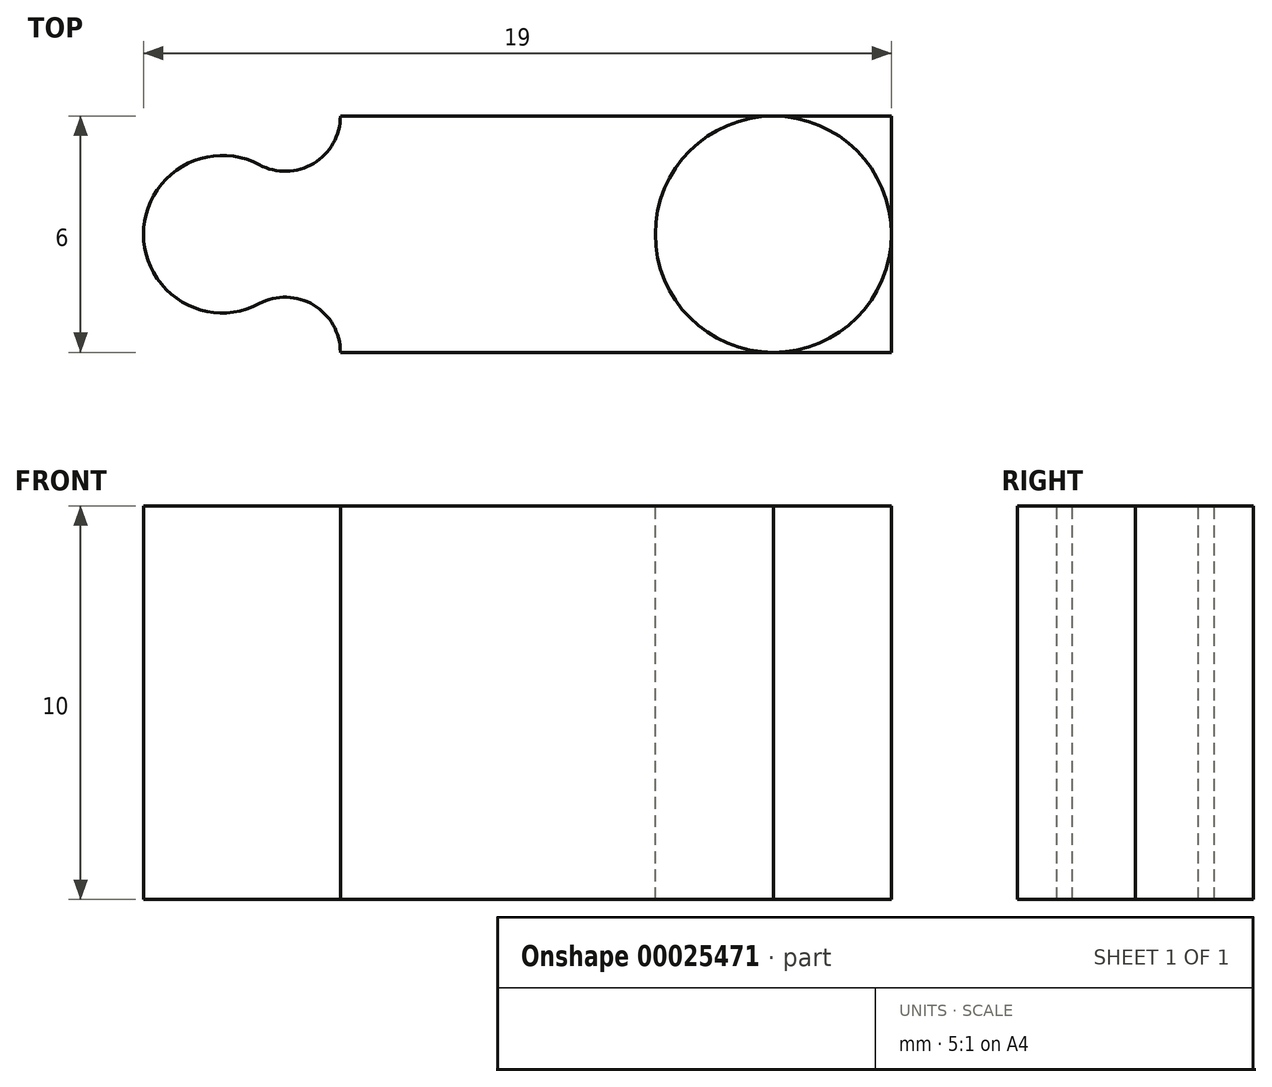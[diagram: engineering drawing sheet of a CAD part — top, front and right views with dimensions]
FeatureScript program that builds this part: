
annotation { "Feature Type Name" : "Feature", "Feature Type Description" : "" }
export const myFeature = defineFeature(function(context is Context, id is Id, definition is map)
    precondition{}
    {
        {
            var Q0;
            Q0=qCreatedBy(makeId("Front.planeOp"),FACE);
            var sketch = newSketch(context, id + "F0", { "sketchPlane" : qUnion([Q0])});
            skLineSegment(sketch, "E0.bottom", {"start": v(0, 0) * mm, "end": v(20, 0) * mm});
            skLineSegment(sketch, "E0.top", {"start": v(0, -10) * mm, "end": v(20, -10) * mm});
            skLineSegment(sketch, "E0.left", {"start": v(0, 0) * mm, "end": v(0, -10) * mm});
            skLineSegment(sketch, "E0.right", {"start": v(20, 0) * mm, "end": v(20, -10) * mm});
            skSolve(sketch);
        }
        {
            var Q0;
            Q0=makeQuery(id+"F0.imprint","IMPRINT",FACE,{"disambiguationData":[TD([[makeQuery(id+"F0.imprint","IMPRINT",EDGE,{"derivedFrom":sQuery(id+"F0.wireOp",EDGE,"E0.bottom")}),-1.0]])]});
            extrude(context, id + "F1", {"entities" : qUnion([Q0]), "depth" : 6 * mm, "symmetric" : true});
        }
        {
            var Q0;
            Q0=makeQuery(id+"F1.opExtrude","SWEPT_FACE",FACE,{"disambiguationData":[OSD([sQuery(id+"F0.wireOp",EDGE,"E0.bottom")])]});
            var sketch = newSketch(context, id + "F2", { "sketchPlane" : qUnion([Q0])});
            skLineSegment(sketch, "E1", {"start": v(-5.02, 0) * mm, "end": v(29.01, 0) * mm, "construction": true});
            skCircle(sketch, "E2", {"center": v(3, 0) * mm, "radius": 3 * mm});
            skCircle(sketch, "E3.0", {"center": v(3, 0) * mm, "radius": 2 * mm});
            skLineSegment(sketch, "E4", {"start": v(6, 3) * mm, "end": v(6, -3) * mm});
            skArc(sketch, "E5", {"start": v(3.94, 1.76) * mm, "mid": v(5.32, 1.8) * mm, "end": v(6, 3) * mm});
            skArc(sketch, "E6.MirrorCS", {"start": v(3.94, -1.76) * mm, "mid": v(5.32, -1.8) * mm, "end": v(6, -3) * mm});
            skLineSegment(sketch, "E7", {"start": v(10, 7.15) * mm, "end": v(10, -6.74) * mm, "construction": true});
            skCircle(sketch, "E8.MirrorC", {"center": v(17, 0) * mm, "radius": 3 * mm});
            skCircle(sketch, "E9.MirrorC", {"center": v(17, 0) * mm, "radius": 2 * mm});
            skLineSegment(sketch, "E10.MirrorCS", {"start": v(14, 3) * mm, "end": v(14, -3) * mm});
            skLineSegment(sketch, "E11", {"start": v(3, 6.84) * mm, "end": v(3, -7.2) * mm, "construction": true});
            skArc(sketch, "E12.MirrorCS", {"start": v(2.06, 1.76) * mm, "mid": v(0.68, 1.8) * mm, "end": v(0, 3) * mm, "construction": true});
            skArc(sketch, "E13.MirrorCS", {"start": v(2.06, -1.76) * mm, "mid": v(0.68, -1.8) * mm, "end": v(0, -3) * mm, "construction": true});
            skArc(sketch, "E14.MirrorCS", {"start": v(17.94, 1.76) * mm, "mid": v(19.32, 1.8) * mm, "end": v(20, 3) * mm});
            skArc(sketch, "E15.MirrorCS", {"start": v(17.94, -1.76) * mm, "mid": v(19.32, -1.8) * mm, "end": v(20, -3) * mm});
            skSolve(sketch);
        }
        {
            var Q0;
            {var subQ0=sQuery(id+"F0.wireOp",EDGE,"E0.bottom");var subQ1=makeQuery(id+"F1.opExtrude","CAP_EDGE",EDGE,{"disambiguationData":[OSD([subQ0])],"isStart":true});var subQ2=sQuery(id+"F2.wireOp",EDGE,"E2");var subQ3=makeQuery(id+"F2.imprint","INTERSECT",VERTEX,{"derivedFrom":[subQ1,subQ2]});Q0=makeQuery(id+"F2.imprint","IMPRINT",FACE,{"disambiguationData":[TD([[makeQuery(id+"F2.imprint","IMPRINT",EDGE,{"disambiguationData":[TD([[subQ3,-1.0]])],"derivedFrom":subQ2}),-1.0]])]});}
            var Q1;
            {var subQ0=sQuery(id+"F0.wireOp",EDGE,"E0.bottom");var subQ1=makeQuery(id+"F1.opExtrude","CAP_EDGE",EDGE,{"disambiguationData":[OSD([subQ0])],"isStart":false});var subQ2=sQuery(id+"F2.wireOp",EDGE,"E2");var subQ3=makeQuery(id+"F2.imprint","INTERSECT",VERTEX,{"derivedFrom":[subQ1,subQ2]});Q1=makeQuery(id+"F2.imprint","IMPRINT",FACE,{"disambiguationData":[TD([[makeQuery(id+"F2.imprint","IMPRINT",EDGE,{"disambiguationData":[TD([[subQ3,1.0]])],"derivedFrom":subQ2}),-1.0]])]});}
            var Q2;
            {var subQ1=sQuery(id+"F2.wireOp",EDGE,"E2");var subQ3=sQuery(id+"F2.wireOp",EDGE,"E6.MirrorCS");var subQ5=makeQuery(id+"F2.imprint","INTERSECT",VERTEX,{"derivedFrom":[subQ1,subQ3]});Q2=makeQuery(id+"F2.imprint","IMPRINT",FACE,{"disambiguationData":[TD([[makeQuery(id+"F2.imprint","IMPRINT",EDGE,{"disambiguationData":[TD([[subQ5,1.0]])],"derivedFrom":subQ1}),-1.0]])]});}
            var Q3;
            {var subQ1=sQuery(id+"F2.wireOp",EDGE,"E2");var subQ5=sQuery(id+"F2.wireOp",EDGE,"E5");var subQ6=makeQuery(id+"F2.imprint","INTERSECT",VERTEX,{"derivedFrom":[subQ1,subQ5]});Q3=makeQuery(id+"F2.imprint","IMPRINT",FACE,{"disambiguationData":[TD([[makeQuery(id+"F2.imprint","IMPRINT",EDGE,{"disambiguationData":[TD([[subQ6,-1.0]])],"derivedFrom":subQ1}),1.0]])]});}
            var Q4;
            {var subQ1=sQuery(id+"F2.wireOp",EDGE,"E2");var subQ3=sQuery(id+"F2.wireOp",EDGE,"E5");var subQ5=makeQuery(id+"F2.imprint","INTERSECT",VERTEX,{"derivedFrom":[subQ1,subQ3]});Q4=makeQuery(id+"F2.imprint","IMPRINT",FACE,{"disambiguationData":[TD([[makeQuery(id+"F2.imprint","IMPRINT",EDGE,{"disambiguationData":[TD([[subQ5,-1.0]])],"derivedFrom":subQ1}),-1.0]])]});}
            var Q5;
            {var subQ2=sQuery(id+"F2.wireOp",EDGE,"E8.MirrorC");var subQ4=sQuery(id+"F2.wireOp",EDGE,"E14.MirrorCS");var subQ6=makeQuery(id+"F2.imprint","INTERSECT",VERTEX,{"derivedFrom":[subQ2,subQ4]});Q5=makeQuery(id+"F2.imprint","IMPRINT",FACE,{"disambiguationData":[TD([[makeQuery(id+"F2.imprint","IMPRINT",EDGE,{"disambiguationData":[TD([[subQ6,1.0]])],"derivedFrom":subQ2}),1.0]])]});}
            var Q6;
            {var subQ2=sQuery(id+"F2.wireOp",EDGE,"E8.MirrorC");var subQ4=sQuery(id+"F2.wireOp",EDGE,"E15.MirrorCS");var subQ6=makeQuery(id+"F2.imprint","INTERSECT",VERTEX,{"derivedFrom":[subQ2,subQ4]});Q6=makeQuery(id+"F2.imprint","IMPRINT",FACE,{"disambiguationData":[TD([[makeQuery(id+"F2.imprint","IMPRINT",EDGE,{"disambiguationData":[TD([[subQ6,-1.0]])],"derivedFrom":subQ2}),1.0]])]});}
            var Q7;
            {var subQ2=sQuery(id+"F2.wireOp",EDGE,"E8.MirrorC");var subQ4=sQuery(id+"F2.wireOp",EDGE,"E15.MirrorCS");var subQ6=makeQuery(id+"F2.imprint","INTERSECT",VERTEX,{"derivedFrom":[subQ2,subQ4]});Q7=makeQuery(id+"F2.imprint","IMPRINT",FACE,{"disambiguationData":[TD([[makeQuery(id+"F2.imprint","IMPRINT",EDGE,{"disambiguationData":[TD([[subQ6,1.0]])],"derivedFrom":subQ2}),1.0]])]});}
            var Q8;
            {var subQ2=sQuery(id+"F2.wireOp",EDGE,"E8.MirrorC");var subQ4=sQuery(id+"F2.wireOp",EDGE,"E14.MirrorCS");var subQ6=makeQuery(id+"F2.imprint","INTERSECT",VERTEX,{"derivedFrom":[subQ2,subQ4]});Q8=makeQuery(id+"F2.imprint","IMPRINT",FACE,{"disambiguationData":[TD([[makeQuery(id+"F2.imprint","IMPRINT",EDGE,{"disambiguationData":[TD([[subQ6,-1.0]])],"derivedFrom":subQ2}),1.0]])]});}
            var Q9;
            {var subQ3=sQuery(id+"F2.wireOp",EDGE,"E9.MirrorC");var subQ5=sQuery(id+"F2.wireOp",EDGE,"E14.MirrorCS");var subQ7=makeQuery(id+"F2.imprint","INTERSECT",VERTEX,{"derivedFrom":[subQ3,subQ5]});Q9=makeQuery(id+"F2.imprint","IMPRINT",FACE,{"disambiguationData":[TD([[makeQuery(id+"F2.imprint","IMPRINT",EDGE,{"disambiguationData":[TD([[subQ7,-1.0]])],"derivedFrom":subQ3}),1.0]])]});}
            var Q10;
            {var subQ0=sQuery(id+"F2.wireOp",EDGE,"E9.MirrorC");var subQ2=makeQuery(id+"F2.imprint","INTERSECT",VERTEX,{"derivedFrom":[subQ0,sQuery(id+"F2.wireOp",EDGE,"E14.MirrorCS")]});Q10=makeQuery(id+"F2.imprint","IMPRINT",FACE,{"disambiguationData":[TD([[makeQuery(id+"F2.imprint","IMPRINT",EDGE,{"disambiguationData":[TD([[subQ2,-1.0]])],"derivedFrom":subQ0}),-1.0]])]});}
            extrude(context, id + "F3", {"entities" : qUnion([Q0, Q1, Q2, Q3, Q4, Q5, Q6, Q7, Q8, Q9, Q10]), "operationType" : NewBodyOperationType.REMOVE, "endBound" : BoundingType.THROUGH_ALL, "oppositeDirection" : true, "depth" : 25 * mm});
        }
    });
